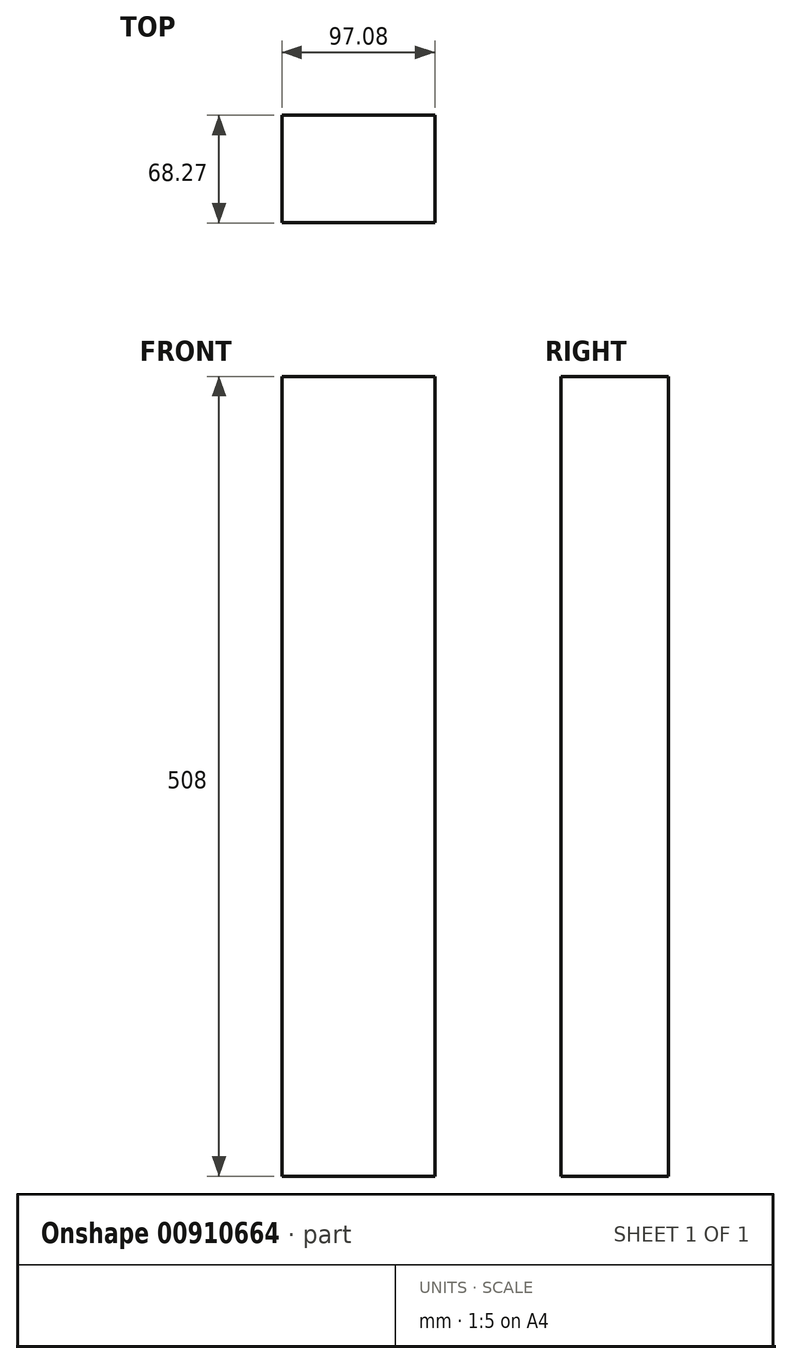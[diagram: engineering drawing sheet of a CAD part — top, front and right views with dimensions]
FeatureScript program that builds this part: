
annotation { "Feature Type Name" : "Feature", "Feature Type Description" : "" }
export const myFeature = defineFeature(function(context is Context, id is Id, definition is map)
    precondition{}
    {
        {
            var Q0;
            Q0=qCreatedBy(makeId("Top.planeOp"),FACE);
            var sketch = newSketch(context, id + "F0", { "sketchPlane" : qUnion([Q0])});
            skLineSegment(sketch, "E0.bottom", {"start": v(-46.19, 32.88) * mm, "end": v(50.89, 32.88) * mm});
            skLineSegment(sketch, "E0.top", {"start": v(-46.19, -35.39) * mm, "end": v(50.89, -35.39) * mm});
            skLineSegment(sketch, "E0.left", {"start": v(-46.19, 32.88) * mm, "end": v(-46.19, -35.39) * mm});
            skLineSegment(sketch, "E0.right", {"start": v(50.89, 32.88) * mm, "end": v(50.89, -35.39) * mm});
            skSolve(sketch);
        }
        {
            var Q0;
            Q0=sQuery(id+"F0.wireOp",EDGE,"E0.right");
            var Q1;
            Q1=sQuery(id+"F0.wireOp",EDGE,"E0.bottom");
            var Q2;
            Q2=sQuery(id+"F0.wireOp",EDGE,"E0.left");
            var Q3;
            Q3=sQuery(id+"F0.wireOp",EDGE,"E0.top");
            extrude(context, id + "F1", {"bodyType" : ToolBodyType.SURFACE, "surfaceEntities" : qUnion([Q0, Q1, Q2, Q3]), "depth" : 508 * mm, "offsetDistance" : 25.4 * mm});
        }
    });
